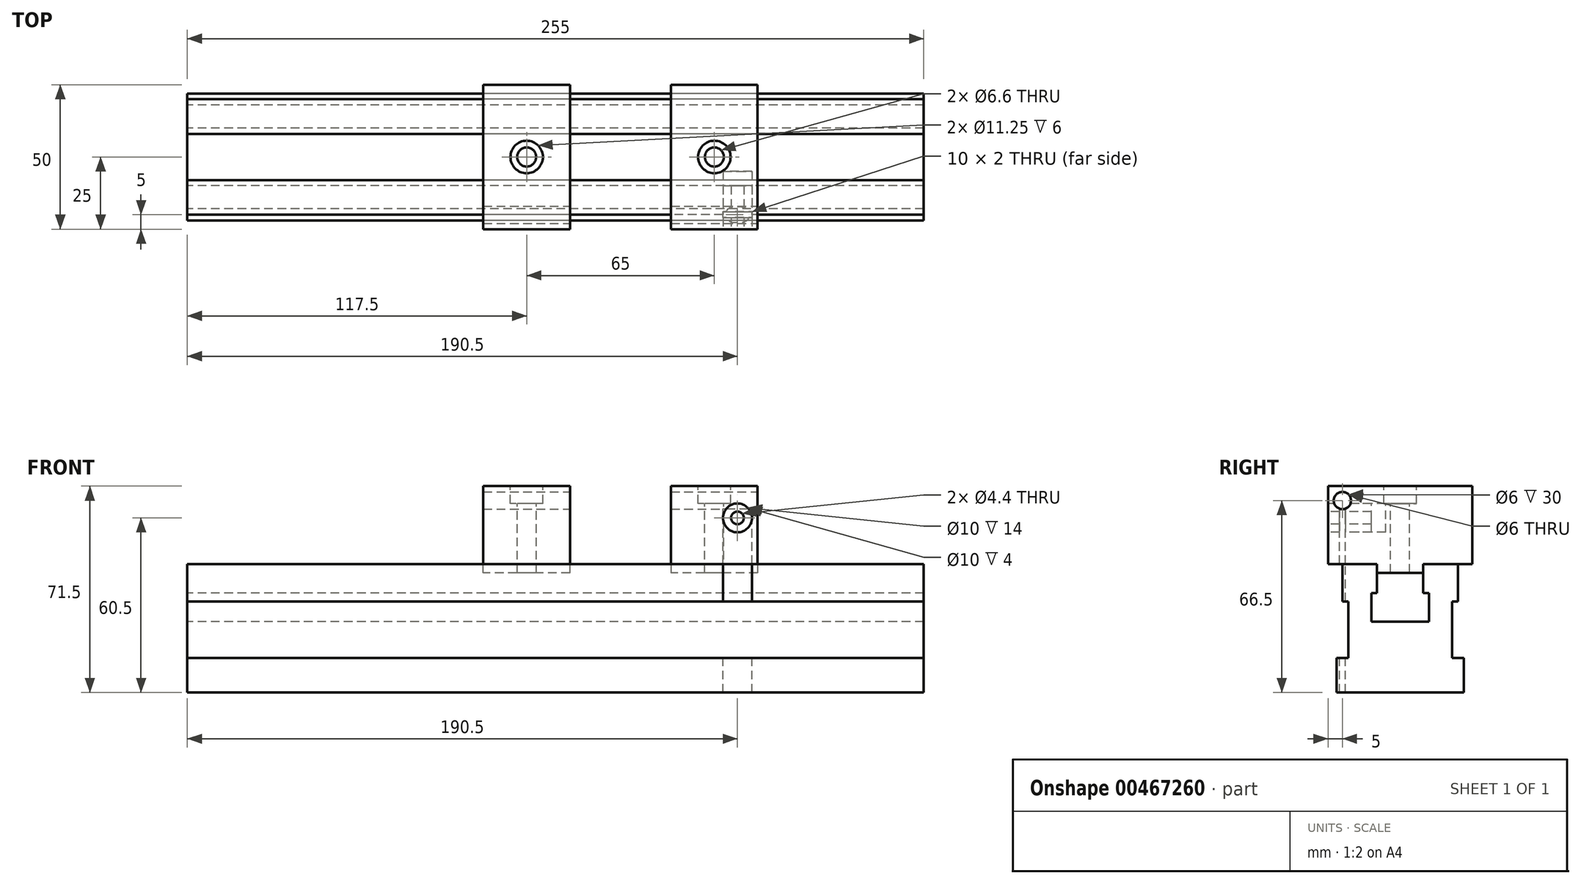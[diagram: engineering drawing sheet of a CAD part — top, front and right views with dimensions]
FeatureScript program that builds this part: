
annotation { "Feature Type Name" : "Feature", "Feature Type Description" : "" }
export const myFeature = defineFeature(function(context is Context, id is Id, definition is map)
    precondition{}
    {
        {
            var Q0;
            Q0=qCreatedBy(makeId("Right.planeOp"),FACE);
            var sketch = newSketch(context, id + "F0", { "sketchPlane" : qUnion([Q0])});
            skLineSegment(sketch, "E0", {"start": v(0, 0) * mm, "end": v(0, 24.5) * mm});
            skLineSegment(sketch, "E1", {"start": v(0, 24.5) * mm, "end": v(10, 24.5) * mm});
            skLineSegment(sketch, "E2", {"start": v(10, 24.5) * mm, "end": v(10, 34.5) * mm});
            skLineSegment(sketch, "E3", {"start": v(10, 34.5) * mm, "end": v(8, 34.5) * mm});
            skLineSegment(sketch, "E4", {"start": v(8, 34.5) * mm, "end": v(8, 44.5) * mm});
            skLineSegment(sketch, "E5", {"start": v(8, 44.5) * mm, "end": v(20, 44.5) * mm});
            skLineSegment(sketch, "E6", {"start": v(20, 44.5) * mm, "end": v(20, 31.56) * mm});
            skLineSegment(sketch, "E7", {"start": v(20, 31.56) * mm, "end": v(18, 31.56) * mm});
            skLineSegment(sketch, "E8", {"start": v(18, 31.56) * mm, "end": v(18, 12) * mm});
            skLineSegment(sketch, "E9", {"start": v(18, 12) * mm, "end": v(22, 12) * mm});
            skLineSegment(sketch, "E10", {"start": v(22, 12) * mm, "end": v(22, 0) * mm});
            skLineSegment(sketch, "E11", {"start": v(22, 0) * mm, "end": v(0, 0) * mm});
            skLineSegment(sketch, "E12.MirrorCS", {"start": v(-10, 34.5) * mm, "end": v(-8, 34.5) * mm});
            skLineSegment(sketch, "E13.MirrorCS", {"start": v(-20, 31.56) * mm, "end": v(-18, 31.56) * mm});
            skLineSegment(sketch, "E14.MirrorCS", {"start": v(-22, 0) * mm, "end": v(0, 0) * mm});
            skLineSegment(sketch, "E15.MirrorCS", {"start": v(0, 24.5) * mm, "end": v(-10, 24.5) * mm});
            skLineSegment(sketch, "E16.MirrorCS", {"start": v(-22, 12) * mm, "end": v(-22, 0) * mm});
            skLineSegment(sketch, "E17.MirrorCS", {"start": v(-18, 12) * mm, "end": v(-22, 12) * mm});
            skLineSegment(sketch, "E18.MirrorCS", {"start": v(-10, 24.5) * mm, "end": v(-10, 34.5) * mm});
            skLineSegment(sketch, "E19.MirrorCS", {"start": v(-20, 44.5) * mm, "end": v(-20, 31.56) * mm});
            skLineSegment(sketch, "E20.MirrorCS", {"start": v(-8, 34.5) * mm, "end": v(-8, 44.5) * mm});
            skLineSegment(sketch, "E21.MirrorCS", {"start": v(-18, 31.56) * mm, "end": v(-18, 12) * mm});
            skLineSegment(sketch, "E22.MirrorCS", {"start": v(-8, 44.5) * mm, "end": v(-20, 44.5) * mm});
            skLineSegment(sketch, "E23.bottom", {"start": v(-25, 44.5) * mm, "end": v(25, 44.5) * mm});
            skLineSegment(sketch, "E23.top", {"start": v(-25, 71.5) * mm, "end": v(25, 71.5) * mm});
            skLineSegment(sketch, "E23.left", {"start": v(-25, 44.5) * mm, "end": v(-25, 71.5) * mm});
            skLineSegment(sketch, "E23.right", {"start": v(25, 44.5) * mm, "end": v(25, 71.5) * mm});
            skLineSegment(sketch, "E24", {"start": v(-8, 41.5) * mm, "end": v(8, 41.5) * mm});
            skSolve(sketch);
        }
        {
            var Q0;
            Q0=makeQuery(id+"F0.imprint","IMPRINT",FACE,{"disambiguationData":[TD([[makeQuery(id+"F0.imprint","IMPRINT",EDGE,{"derivedFrom":sQuery(id+"F0.wireOp",EDGE,"E0")}),1.0]])]});
            var Q1;
            Q1=makeQuery(id+"F0.imprint","IMPRINT",FACE,{"disambiguationData":[TD([[makeQuery(id+"F0.imprint","IMPRINT",EDGE,{"derivedFrom":sQuery(id+"F0.wireOp",EDGE,"E0")}),-1.0]])]});
            extrude(context, id + "F1", {"entities" : qUnion([Q0, Q1]), "endBound" : BoundingType.SYMMETRIC, "depth" : 255 * mm});
        }
        {
            var Q0;
            Q0=qCreatedBy(makeId("Right.planeOp"),FACE);
            cPlane(context, id + "F2", {"entities" : qUnion([Q0]), "cplaneType" : CPlaneType.OFFSET, "offset" : 40 * mm, "width" : 150 * mm, "height" : 150 * mm});
        }
        {
            var Q0;
            Q0=qCreatedBy(makeId("Right.planeOp"),FACE);
            cPlane(context, id + "F3", {"entities" : qUnion([Q0]), "cplaneType" : CPlaneType.OFFSET, "offset" : 25 * mm, "oppositeDirection" : true, "width" : 150 * mm, "height" : 150 * mm});
        }
        {
            var Q0;
            Q0=qCreatedBy(id+"F2.planeOp",FACE);
            var sketch = newSketch(context, id + "F4", { "sketchPlane" : qUnion([Q0])});
            skLineSegment(sketch, "E25.0", {"start": v(-25, 44.5) * mm, "end": v(-25, 71.5) * mm});
            skLineSegment(sketch, "E26.0", {"start": v(25, 44.5) * mm, "end": v(25, 71.5) * mm});
            skLineSegment(sketch, "E27.0", {"start": v(-25, 71.5) * mm, "end": v(25, 71.5) * mm});
            skLineSegment(sketch, "E28.0", {"start": v(-8, 41.5) * mm, "end": v(8, 41.5) * mm});
            skLineSegment(sketch, "E29", {"start": v(-25, 44.5) * mm, "end": v(-8, 44.5) * mm});
            skLineSegment(sketch, "E30", {"start": v(-8, 44.5) * mm, "end": v(-8, 41.5) * mm});
            skLineSegment(sketch, "E31", {"start": v(25, 44.5) * mm, "end": v(8, 44.5) * mm});
            skLineSegment(sketch, "E32", {"start": v(8, 44.5) * mm, "end": v(8, 41.5) * mm});
            skSolve(sketch);
        }
        {
            var Q0;
            Q0=makeQuery(id+"F4.imprint","IMPRINT",FACE,{"disambiguationData":[TD([[makeQuery(id+"F4.imprint","IMPRINT",EDGE,{"derivedFrom":sQuery(id+"F4.wireOp",EDGE,"E25.0")}),-1.0]])]});
            extrude(context, id + "F5", {"entities" : qUnion([Q0]), "depth" : 30 * mm});
        }
        {
            var Q0;
            Q0=qCreatedBy(id+"F3.planeOp",FACE);
            var sketch = newSketch(context, id + "F6", { "sketchPlane" : qUnion([Q0])});
            skLineSegment(sketch, "E33.0.0", {"start": v(8, 41.5) * mm, "end": v(8, 44.5) * mm});
            skLineSegment(sketch, "E33.0.1", {"start": v(8, 44.5) * mm, "end": v(20, 44.5) * mm});
            skLineSegment(sketch, "E33.0.2", {"start": v(20, 44.5) * mm, "end": v(25, 44.5) * mm});
            skLineSegment(sketch, "E33.0.3", {"start": v(25, 44.5) * mm, "end": v(25, 71.5) * mm});
            skLineSegment(sketch, "E33.0.4", {"start": v(25, 71.5) * mm, "end": v(-25, 71.5) * mm});
            skLineSegment(sketch, "E33.0.5", {"start": v(-25, 71.5) * mm, "end": v(-25, 44.5) * mm});
            skLineSegment(sketch, "E33.0.6", {"start": v(-25, 44.5) * mm, "end": v(-20, 44.5) * mm});
            skLineSegment(sketch, "E33.0.7", {"start": v(-20, 44.5) * mm, "end": v(-8, 44.5) * mm});
            skLineSegment(sketch, "E33.0.8", {"start": v(-8, 44.5) * mm, "end": v(-8, 41.5) * mm});
            skLineSegment(sketch, "E33.0.9", {"start": v(-8, 41.5) * mm, "end": v(8, 41.5) * mm});
            skSolve(sketch);
        }
        {
            var Q0;
            Q0=makeQuery(id+"F6.imprint","IMPRINT",FACE,{"disambiguationData":[TD([[makeQuery(id+"F6.imprint","IMPRINT",EDGE,{"derivedFrom":sQuery(id+"F6.wireOp",EDGE,"E33.0.0")}),1.0]])]});
            extrude(context, id + "F7", {"entities" : qUnion([Q0]), "depth" : 30 * mm});
        }
        {
            var Q0;
            Q0=makeQuery(id+"F5.opExtrude","CAP_FACE",FACE,{"disambiguationData":[OSD([sQuery(id+"F4.wireOp",EDGE,"E25.0"),sQuery(id+"F4.wireOp",EDGE,"E26.0"),sQuery(id+"F4.wireOp",EDGE,"E27.0"),sQuery(id+"F4.wireOp",EDGE,"E28.0"),sQuery(id+"F4.wireOp",EDGE,"E29"),sQuery(id+"F4.wireOp",EDGE,"E30"),sQuery(id+"F4.wireOp",EDGE,"E31"),sQuery(id+"F4.wireOp",EDGE,"E32")])],"isStart":false});
            var sketch = newSketch(context, id + "F8", { "sketchPlane" : qUnion([Q0])});
            skCircle(sketch, "E34", {"center": v(-20, 66.5) * mm, "radius": 3 * mm});
            skSolve(sketch);
        }
        {
            var Q0;
            Q0=makeQuery(id+"F8.imprint","IMPRINT",FACE,{"disambiguationData":[TD([[makeQuery(id+"F8.imprint","IMPRINT",EDGE,{"derivedFrom":sQuery(id+"F8.wireOp",EDGE,"E34")}),1.0]])]});
            extrude(context, id + "F9", {"entities" : qUnion([Q0]), "operationType" : NewBodyOperationType.REMOVE, "endBound" : BoundingType.THROUGH_ALL, "oppositeDirection" : true, "depth" : 25 * mm});
        }
        {
            var Q0;
            Q0=makeQuery(id+"F7.opExtrude","CAP_FACE",FACE,{"disambiguationData":[OSD([sQuery(id+"F6.wireOp",EDGE,"E33.0.0"),sQuery(id+"F6.wireOp",EDGE,"E33.0.1"),sQuery(id+"F6.wireOp",EDGE,"E33.0.2"),sQuery(id+"F6.wireOp",EDGE,"E33.0.3"),sQuery(id+"F6.wireOp",EDGE,"E33.0.4"),sQuery(id+"F6.wireOp",EDGE,"E33.0.5"),sQuery(id+"F6.wireOp",EDGE,"E33.0.6"),sQuery(id+"F6.wireOp",EDGE,"E33.0.7"),sQuery(id+"F6.wireOp",EDGE,"E33.0.8"),sQuery(id+"F6.wireOp",EDGE,"E33.0.9")])],"isStart":false});
            var sketch = newSketch(context, id + "F10", { "sketchPlane" : qUnion([Q0])});
            skCircle(sketch, "E35.0", {"center": v(-20, 66.5) * mm, "radius": 3 * mm});
            skSolve(sketch);
        }
        {
            var Q0;
            Q0=makeQuery(id+"F10.imprint","IMPRINT",FACE,{"disambiguationData":[TD([[makeQuery(id+"F10.imprint","IMPRINT",EDGE,{"derivedFrom":sQuery(id+"F10.wireOp",EDGE,"E35.0")}),1.0]])]});
            extrude(context, id + "F11", {"entities" : qUnion([Q0]), "operationType" : NewBodyOperationType.REMOVE, "endBound" : BoundingType.THROUGH_ALL, "oppositeDirection" : true, "depth" : 25 * mm});
        }
        {
            var Q0;
            Q0=makeQuery(id+"F5.opExtrude","SWEPT_FACE",FACE,{"disambiguationData":[OSD([sQuery(id+"F4.wireOp",EDGE,"E27.0")])]});
            var sketch = newSketch(context, id + "F12", { "sketchPlane" : qUnion([Q0])});
            skLineSegment(sketch, "E36", {"start": v(40, -25) * mm, "end": v(70, 25) * mm});
            skLineSegment(sketch, "E37", {"start": v(70, 25) * mm, "end": v(40, 25) * mm});
            skLineSegment(sketch, "E38", {"start": v(40, 25) * mm, "end": v(70, -25) * mm});
            skPoint(sketch, "E39", {"position": v(55, 0) * mm});
            skSolve(sketch);
        }
        {
            var Q0;
            Q0=makeQuery(id+"F7.opExtrude","SWEPT_FACE",FACE,{"disambiguationData":[OSD([sQuery(id+"F6.wireOp",EDGE,"E33.0.4")])]});
            var sketch = newSketch(context, id + "F13", { "sketchPlane" : qUnion([Q0])});
            skLineSegment(sketch, "E40", {"start": v(-25, -25) * mm, "end": v(5, 25) * mm});
            skLineSegment(sketch, "E41", {"start": v(5, 25) * mm, "end": v(-25, 25) * mm});
            skLineSegment(sketch, "E42", {"start": v(-25, 25) * mm, "end": v(5, -25) * mm});
            skPoint(sketch, "E43", {"position": v(-10, 0) * mm});
            skSolve(sketch);
        }
        {
            var Q0;
            Q0=sQuery(id+"F13.wireOp",VERTEX,"E43");
            var Q1;
            Q1=makeQuery(id+"F7.opExtrude","SWEPT_BODY",BODY,{"disambiguationData":[OSD([sQuery(id+"F6.wireOp",EDGE,"E33.0.0"),sQuery(id+"F6.wireOp",EDGE,"E33.0.1"),sQuery(id+"F6.wireOp",EDGE,"E33.0.2"),sQuery(id+"F6.wireOp",EDGE,"E33.0.3"),sQuery(id+"F6.wireOp",EDGE,"E33.0.4"),sQuery(id+"F6.wireOp",EDGE,"E33.0.5"),sQuery(id+"F6.wireOp",EDGE,"E33.0.6"),sQuery(id+"F6.wireOp",EDGE,"E33.0.7"),sQuery(id+"F6.wireOp",EDGE,"E33.0.8"),sQuery(id+"F6.wireOp",EDGE,"E33.0.9")])]});
            hole(context, id + "F14", {"style" : HoleStyle.C_BORE, "endStyle" : HoleEndStyle.THROUGH, "standardTappedOrClearance" : lookupTablePath({ "standard" : "ISO", "fit" : "Normal", "size" : "M6", "type" : "Clearance" }), "standardBlindInLast" : lookupTablePath({ "fit" : "Standard", "standard" : "ISO", "size" : "M6", "type" : "Clearance" }), "holeDiameter" : 6.6 * mm, "cBoreDiameter" : 11.25 * mm, "cBoreDepth" : 6 * mm, "isTappedThrough" : true, "tappedDepth" : 12 * mm, "tapClearance" : 3, "locations" : qUnion([Q0]), "scope" : qUnion([Q1])});
        }
        {
            var Q0;
            Q0=sQuery(id+"F12.wireOp",VERTEX,"E39");
            var Q1;
            Q1=makeQuery(id+"F5.opExtrude","SWEPT_BODY",BODY,{"disambiguationData":[OSD([sQuery(id+"F4.wireOp",EDGE,"E25.0"),sQuery(id+"F4.wireOp",EDGE,"E26.0"),sQuery(id+"F4.wireOp",EDGE,"E27.0"),sQuery(id+"F4.wireOp",EDGE,"E28.0"),sQuery(id+"F4.wireOp",EDGE,"E29"),sQuery(id+"F4.wireOp",EDGE,"E30"),sQuery(id+"F4.wireOp",EDGE,"E31"),sQuery(id+"F4.wireOp",EDGE,"E32")])]});
            hole(context, id + "F15", {"style" : HoleStyle.C_BORE, "endStyle" : HoleEndStyle.THROUGH, "standardTappedOrClearance" : lookupTablePath({ "standard" : "ISO", "fit" : "Normal", "size" : "M6", "type" : "Clearance" }), "standardBlindInLast" : lookupTablePath({ "fit" : "Standard", "standard" : "ISO", "size" : "M6", "type" : "Clearance" }), "holeDiameter" : 6.6 * mm, "cBoreDiameter" : 11.25 * mm, "cBoreDepth" : 6 * mm, "isTappedThrough" : true, "tappedDepth" : 12 * mm, "tapClearance" : 3, "locations" : qUnion([Q0]), "scope" : qUnion([Q1])});
        }
        {
            var Q0;
            Q0=makeQuery(id+"F5.opExtrude","SWEPT_FACE",FACE,{"disambiguationData":[OSD([sQuery(id+"F4.wireOp",EDGE,"E27.0")])]});
            cPlane(context, id + "F16", {"entities" : qUnion([Q0]), "cplaneType" : CPlaneType.OFFSET, "offset" : 5 * mm, "oppositeDirection" : true, "width" : 150 * mm, "height" : 150 * mm});
        }
        {
            var Q0;
            Q0=qCreatedBy(id+"F16.planeOp",FACE);
            var sketch = newSketch(context, id + "F17", { "sketchPlane" : qUnion([Q0])});
            skPoint(sketch, "E44.0", {"position": v(0, -20) * mm});
            skLineSegment(sketch, "E45", {"start": v(-41.57, -20) * mm, "end": v(98.68, -20) * mm});
            skLineSegment(sketch, "E46", {"start": v(75, -20) * mm, "end": v(75, -23) * mm});
            skLineSegment(sketch, "E47", {"start": v(75, -23) * mm, "end": v(35.2, -23) * mm});
            skLineSegment(sketch, "E48", {"start": v(35.2, -23) * mm, "end": v(30, -20) * mm});
            skLineSegment(sketch, "E49", {"start": v(30, -20) * mm, "end": v(75, -20) * mm});
            skLineSegment(sketch, "E50", {"start": v(15, -20) * mm, "end": v(9.8, -23) * mm});
            skLineSegment(sketch, "E51", {"start": v(9.8, -23) * mm, "end": v(-30, -23) * mm});
            skLineSegment(sketch, "E52", {"start": v(-30, -23) * mm, "end": v(-30, -20) * mm});
            skLineSegment(sketch, "E53", {"start": v(-30, -20) * mm, "end": v(15, -20) * mm});
            skSolve(sketch);
        }
        {
            var Q0;
            Q0=makeQuery(id+"F17.imprint","IMPRINT",FACE,{"disambiguationData":[TD([[makeQuery(id+"F17.imprint","IMPRINT",EDGE,{"derivedFrom":sQuery(id+"F17.wireOp",EDGE,"E46")}),-1.0]])]});
            var Q1;
            Q1=sQuery(id+"F17.wireOp",EDGE,"E45");
            revolve(context, id + "F18", {"entities" : qUnion([Q0]), "axis" : qUnion([Q1]), "revolveType" : RevolveType.FULL});
        }
        {
            var Q0;
            Q0=makeQuery(id+"F17.imprint","IMPRINT",FACE,{"disambiguationData":[TD([[makeQuery(id+"F17.imprint","IMPRINT",EDGE,{"derivedFrom":sQuery(id+"F17.wireOp",EDGE,"E50")}),-1.0]])]});
            var Q1;
            Q1=sQuery(id+"F17.wireOp",EDGE,"E53");
            revolve(context, id + "F19", {"entities" : qUnion([Q0]), "axis" : qUnion([Q1]), "revolveType" : RevolveType.FULL});
        }
        {
            var Q0;
            Q0=makeQuery(id+"F5.opExtrude","SWEPT_FACE",FACE,{"disambiguationData":[OSD([sQuery(id+"F4.wireOp",EDGE,"E25.0")])]});
            var sketch = newSketch(context, id + "F20", { "sketchPlane" : qUnion([Q0])});
            skCircle(sketch, "E54", {"center": v(63, 60.5) * mm, "radius": 5 * mm});
            skCircle(sketch, "E55", {"center": v(63, 60.5) * mm, "radius": 2 * mm});
            skLineSegment(sketch, "E56.0", {"start": v(75, 63.5) * mm, "end": v(75, 69.5) * mm});
            skSolve(sketch);
        }
        {
            var Q0;
            Q0=makeQuery(id+"F20.imprint","IMPRINT",FACE,{"disambiguationData":[TD([[makeQuery(id+"F20.imprint","IMPRINT",EDGE,{"derivedFrom":sQuery(id+"F20.wireOp",EDGE,"E54")}),1.0]])]});
            var Q1;
            Q1=makeQuery(id+"F20.imprint","IMPRINT",FACE,{"disambiguationData":[TD([[makeQuery(id+"F20.imprint","IMPRINT",EDGE,{"derivedFrom":sQuery(id+"F20.wireOp",EDGE,"E55")}),1.0]])]});
            extrude(context, id + "F21", {"entities" : qUnion([Q0, Q1]), "operationType" : NewBodyOperationType.REMOVE, "oppositeDirection" : true, "depth" : 20 * mm});
        }
        {
            var Q0;
            Q0=makeQuery(id+"F20.imprint","IMPRINT",FACE,{"disambiguationData":[TD([[makeQuery(id+"F20.imprint","IMPRINT",EDGE,{"derivedFrom":sQuery(id+"F20.wireOp",EDGE,"E54")}),1.0]])]});
            var Q1;
            Q1=makeQuery(id+"F20.imprint","IMPRINT",FACE,{"disambiguationData":[TD([[makeQuery(id+"F20.imprint","IMPRINT",EDGE,{"derivedFrom":sQuery(id+"F20.wireOp",EDGE,"E55")}),1.0]])]});
            extrude(context, id + "F22", {"entities" : qUnion([Q0, Q1]), "oppositeDirection" : true, "depth" : 15 * mm});
        }
        {
            var Q0;
            Q0=sQuery(id+"F20.wireOp",VERTEX,"E54.center");
            var Q1;
            Q1=makeQuery(id+"F22.opExtrude","SWEPT_BODY",BODY,{"disambiguationData":[OSD([sQuery(id+"F20.wireOp",EDGE,"E54")])]});
            hole(context, id + "F23", {"style" : HoleStyle.SIMPLE, "endStyle" : HoleEndStyle.THROUGH, "standardTappedOrClearance" : lookupTablePath({ "standard" : "ISO", "fit" : "Normal", "size" : "M4", "type" : "Clearance" }), "standardBlindInLast" : lookupTablePath({ "fit" : "Standard", "standard" : "ISO", "size" : "M4", "type" : "Clearance" }), "holeDiameter" : 4.4 * mm, "isTappedThrough" : true, "tappedDepth" : 12 * mm, "tapClearance" : 3, "locations" : qUnion([Q0]), "scope" : qUnion([Q1])});
        }
        {
            var Q0;
            Q0=makeQuery(id+"F18.opRevolve","SWEPT_FACE",FACE,{"disambiguationData":[OSD([sQuery(id+"F17.wireOp",EDGE,"E46")])]});
            extrude(context, id + "F24", {"entities" : qUnion([Q0]), "operationType" : NewBodyOperationType.REMOVE, "endBound" : BoundingType.THROUGH_ALL, "oppositeDirection" : true, "depth" : 25 * mm});
        }
        {
            var Q0;
            Q0=qCreatedBy(id+"F16.planeOp",FACE);
            var sketch = newSketch(context, id + "F25", { "sketchPlane" : qUnion([Q0])});
            skLineSegment(sketch, "E57", {"start": v(58, -25) * mm, "end": v(58, -10) * mm});
            skLineSegment(sketch, "E58", {"start": v(68, -10) * mm, "end": v(68, -25) * mm});
            skLineSegment(sketch, "E59", {"start": v(58, -21) * mm, "end": v(68, -21) * mm});
            skLineSegment(sketch, "E60", {"start": v(58, -19) * mm, "end": v(68, -19) * mm});
            skSolve(sketch);
        }
        {
            var Q0;
            {var subQ0=sQuery(id+"F25.wireOp",EDGE,"E59");Q0=makeQuery(id+"F25.imprint","IMPRINT",FACE,{"disambiguationData":[TD([[makeQuery(id+"F25.imprint","IMPRINT",EDGE,{"derivedFrom":subQ0}),1.0]])]});}
            extrude(context, id + "F26", {"entities" : qUnion([Q0]), "operationType" : NewBodyOperationType.REMOVE, "endBound" : BoundingType.THROUGH_ALL, "oppositeDirection" : true, "depth" : 25 * mm});
        }
    });
